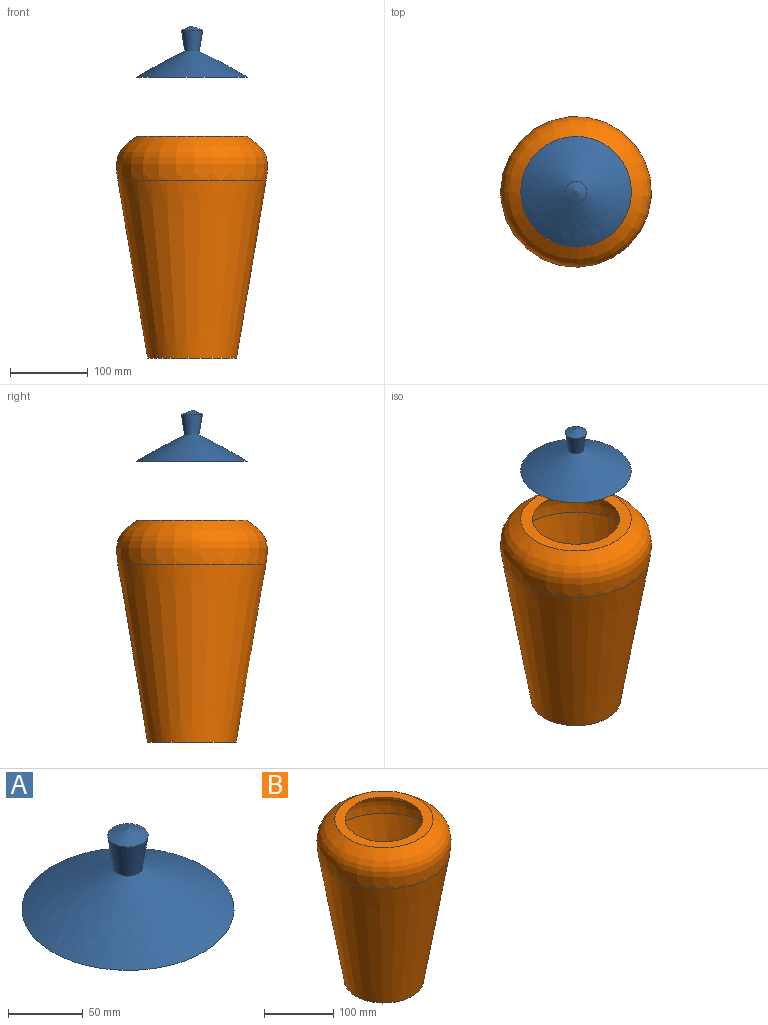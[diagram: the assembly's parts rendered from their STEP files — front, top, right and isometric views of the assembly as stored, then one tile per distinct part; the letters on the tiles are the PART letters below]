
ASSEMBLY  parts=2 mates=1
PART A: 6 faces, bbox 142x142x65.9 mm
  f0: cone r=7.05mm half-angle=81.4deg, axis (0,0,-1), area 157.7mm2, adj f1
  f1: revolved ~111.69x111.69mm, area 10968.9mm2, adj f0,f2
  f2: plane 141.96x141.96mm, normal (0,0,-1), area 6029.5mm2, adj f1,f5
  f3: cone r=13.54mm half-angle=68deg, axis (0,0,-1), area 620.9mm2, adj f4
  f4: cone r=9.53mm half-angle=8.6deg, axis (0,0,1), area 1955.4mm2, adj f3,f5
  f5: revolved ~141.96x141.96mm, area 17856.5mm2, adj f2,f4
PART B: 7 faces, bbox 194x194x284.6 mm
  f0: revolved ~178.33x178.33mm, area 66559.8mm2, adj f2,f3
  f1: plane 100.75x100.75mm, normal (0,0,1), area 7971.6mm2, adj f2
  f2: cone r=87.93mm half-angle=9.5deg, axis (0,0,1), area 99266mm2, adj f0,f1
  f3: plane 141.96x141.96mm, normal (0,0,1), area 6029.5mm2, adj f0,f4
  f4: revolved ~193.99x193.99mm, area 75391.9mm2, adj f3,f6
  f5: plane 114.3x114.3mm, normal (0,0,-1), area 10260.8mm2, adj f6
  f6: cone r=95.25mm half-angle=9.5deg, axis (0,0,1), area 110958.5mm2, adj f4,f5
PLACE A t=(0,0,75.93)mm
PLACE B at identity
MATE slider A.f0 <-> B.f2  axis (0,0,-1) through (0,0,360.51)mm
